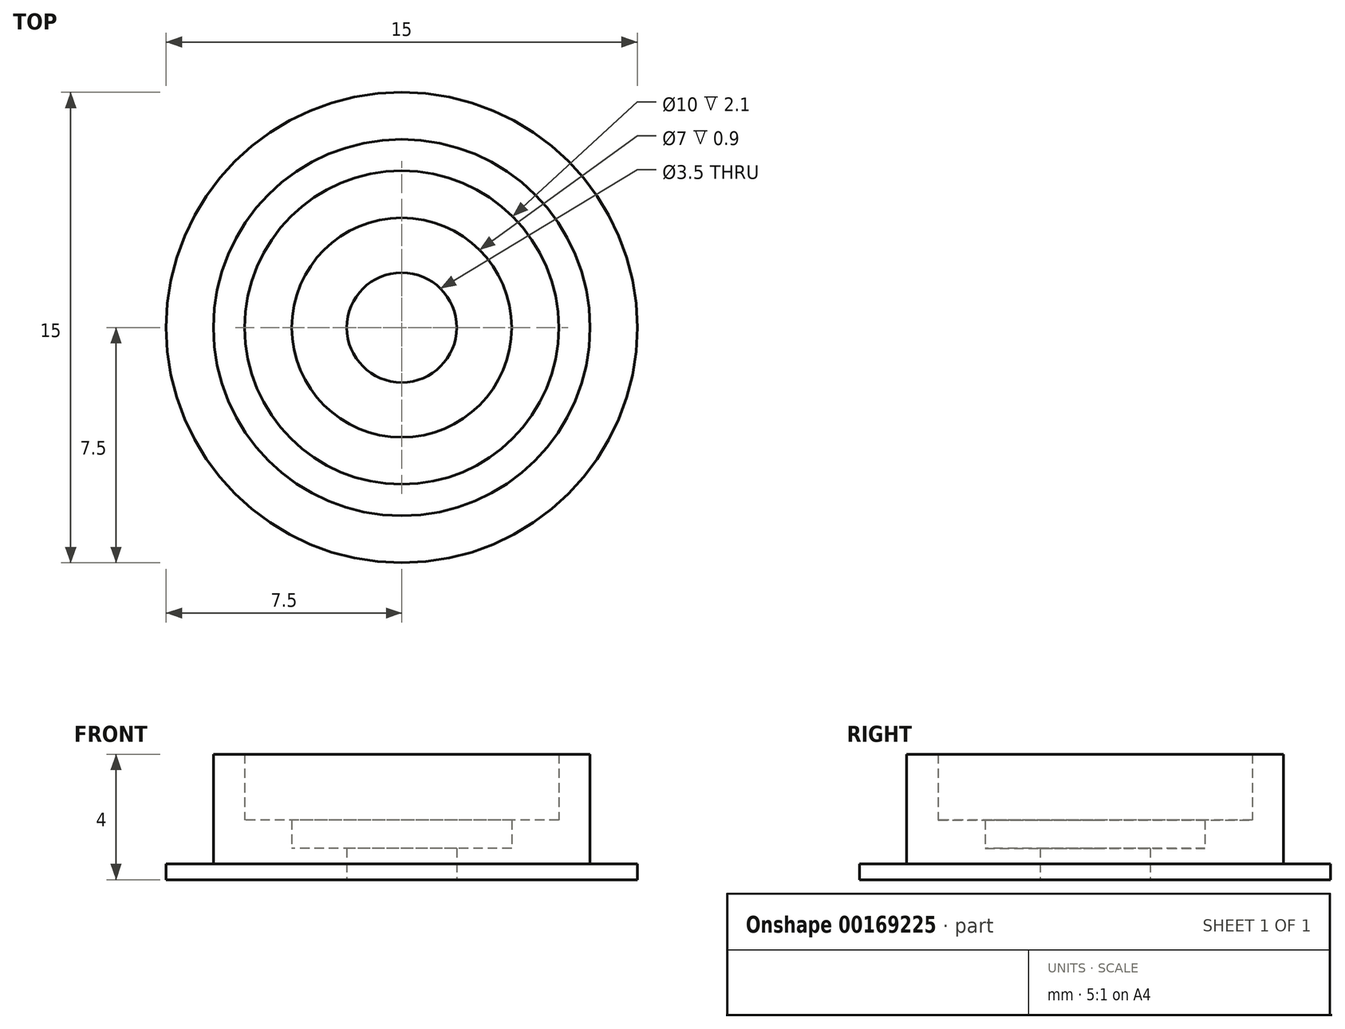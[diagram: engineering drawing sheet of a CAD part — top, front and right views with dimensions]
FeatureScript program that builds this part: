
annotation { "Feature Type Name" : "Feature", "Feature Type Description" : "" }
export const myFeature = defineFeature(function(context is Context, id is Id, definition is map)
    precondition{}
    {
        {
            var Q0;
            Q0=qCreatedBy(makeId("Top.planeOp"),FACE);
            var sketch = newSketch(context, id + "F0", { "sketchPlane" : qUnion([Q0])});
            skCircle(sketch, "E0", {"center": v(0, 0) * mm, "radius": 6 * mm});
            skCircle(sketch, "E1", {"center": v(0, 0) * mm, "radius": 1.75 * mm});
            skCircle(sketch, "E2.0", {"center": v(0, 0) * mm, "radius": 7.5 * mm});
            skCircle(sketch, "E3", {"center": v(0, 0) * mm, "radius": 3.5 * mm});
            skCircle(sketch, "E4", {"center": v(0, 0) * mm, "radius": 5 * mm});
            skSolve(sketch);
        }
        {
            var Q0;
            Q0=makeQuery(id+"F0.imprint","IMPRINT",FACE,{"disambiguationData":[TD([[makeQuery(id+"F0.imprint","IMPRINT",EDGE,{"derivedFrom":sQuery(id+"F0.wireOp",EDGE,"E0")}),1.0]])]});
            extrude(context, id + "F1", {"entities" : qUnion([Q0]), "depth" : 4 * mm, "offsetDistance" : 25 * mm});
        }
        {
            var Q0;
            Q0 = qSketchRegion(id + "F0", true);
            extrude(context, id + "F2", {"entities" : qUnion([Q0]), "operationType" : NewBodyOperationType.ADD, "depth" : 0.5 * mm, "offsetDistance" : 25 * mm});
        }
        {
            var Q0;
            Q0=makeQuery(id+"F0.imprint","IMPRINT",FACE,{"disambiguationData":[TD([[makeQuery(id+"F0.imprint","IMPRINT",EDGE,{"derivedFrom":sQuery(id+"F0.wireOp",EDGE,"E3")}),-1.0]])]});
            var Q1;
            Q1=makeQuery(id+"F1.opExtrude","CAP_FACE",FACE,{"disambiguationData":[OSD([sQuery(id+"F0.wireOp",EDGE,"E0"),sQuery(id+"F0.wireOp",EDGE,"E4")])],"isStart":false});
            extrude(context, id + "F3", {"entities" : qUnion([Q0]), "operationType" : NewBodyOperationType.ADD, "endBound" : BoundingType.UP_TO_SURFACE, "depth" : 25 * mm, "endBoundEntityFace" : qUnion([Q1]), "hasOffset" : true, "offsetDistance" : 2.1 * mm});
        }
        {
            var Q0;
            Q0=makeQuery(id+"F0.imprint","IMPRINT",FACE,{"disambiguationData":[TD([[makeQuery(id+"F0.imprint","IMPRINT",EDGE,{"derivedFrom":sQuery(id+"F0.wireOp",EDGE,"E1")}),-1.0]])]});
            extrude(context, id + "F4", {"entities" : qUnion([Q0]), "operationType" : NewBodyOperationType.ADD, "depth" : 1 * mm, "offsetDistance" : 25 * mm});
        }
    });
